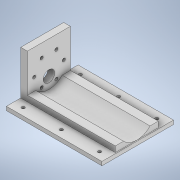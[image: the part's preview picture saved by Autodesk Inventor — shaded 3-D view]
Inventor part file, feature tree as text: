
AUTODESK INVENTOR PART (.ipt)
format: ipt  version: 2020.1 (Build 241239000, 239)  size: 189,440 bytes
history: native  units: mm
features: sketch x7, extrude x4, hole x2
ambient origin geometry x8: Origin, YZ Plane, XZ Plane, XY Plane, X Axis, Y Axis, Z Axis, Center Point
bodies: Solid1 (feature_tree)
feature tree (13):
  extrude  "Extrusion1"  Depth=50.0mm
  extrude  "Extrusion2"  Depth=92.0mm
  hole  "Hole1"  [1 undecoded]
  sketch  "Sketch5"  dims[d8=23.0mm d9=22.5mm]
  extrude  "Extrusion3"  Depth=22.5mm
  extrude  "Extrusion4"  Depth=10.0mm
  hole  "Hole2"  [1 undecoded]
  sketch  "Sketch1"  dims[d0=10.0mm d1=50.0mm]
  sketch  "Sketch3"  dims[d2=7.0mm d4=92.0mm]
  sketch  "Sketch4"  dims[d5=45.0mm d6=0.0mm d7=38.0mm]
  sketch  "Sketch6"  dims[d10=10.0mm d11=0.0mm d12=38.0mm]
  sketch  "Sketch7"  dims[d13=7.0mm d14=6.5mm]
  sketch  "Sketch8"  dims[d15=22.5mm d16=31.0mm d17=60.0deg d18=60.0deg d19=60.0deg d20=60.0deg d21=3.3mm d22=6.0mm d23=4.0mm d24=2.0mm d25=90.0deg d26=8.0mm d27=20.594885mm d28=12.0mm d29=22.5mm d30=7.0mm d31=140.0mm d32=0.0mm d33=4.0mm d34=15.0mm d35=0.0mm d36=60.0mm d37=0.0mm d38=7.5mm d39=10.0mm d40=10.0mm d41=7.5mm d42=10.0mm d43=7.5mm d44=10.0mm d45=7.5mm d46=3.3mm d47=6.0mm d48=4.0mm d49=2.0mm d50=90.0deg d51=8.0mm d52=20.594885mm d53=50.0mm d54=50.0mm d55=100.0mm]
note: 2 required parameter values undecoded (feature->parameter linkage not recoverable at this tier; creation-order binding heuristic only, values carry confidence <= 0.55)
